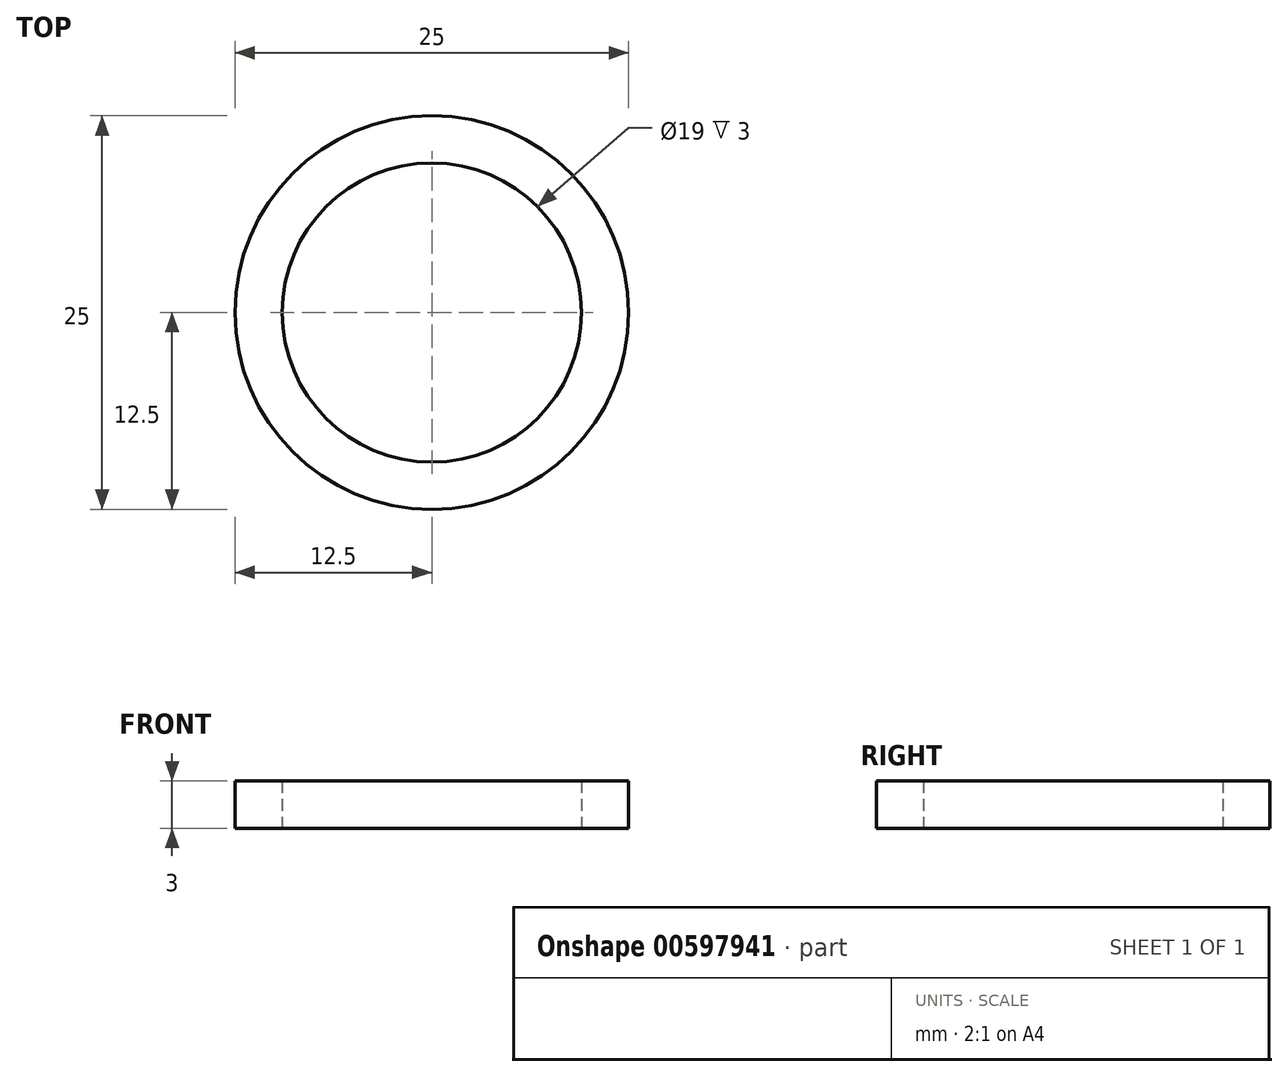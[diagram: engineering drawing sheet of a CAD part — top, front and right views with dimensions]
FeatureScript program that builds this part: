
annotation { "Feature Type Name" : "Feature", "Feature Type Description" : "" }
export const myFeature = defineFeature(function(context is Context, id is Id, definition is map)
    precondition{}
    {
        {
            var Q0;
            Q0=qCreatedBy(makeId("Top.planeOp"),FACE);
            var sketch = newSketch(context, id + "F0", { "sketchPlane" : qUnion([Q0])});
            skCircle(sketch, "E0", {"center": v(0, 0) * mm, "radius": 9.5 * mm});
            skCircle(sketch, "E1.0", {"center": v(0, 0) * mm, "radius": 12.5 * mm});
            skSolve(sketch);
        }
        {
            var Q0;
            Q0=makeQuery(id+"F0.imprint","IMPRINT",FACE,{"disambiguationData":[TD([[makeQuery(id+"F0.imprint","IMPRINT",EDGE,{"derivedFrom":sQuery(id+"F0.wireOp",EDGE,"E0")}),-1.0]])]});
            extrude(context, id + "F1", {"entities" : qUnion([Q0]), "depth" : 3 * mm, "offsetDistance" : 25 * mm});
        }
    });
